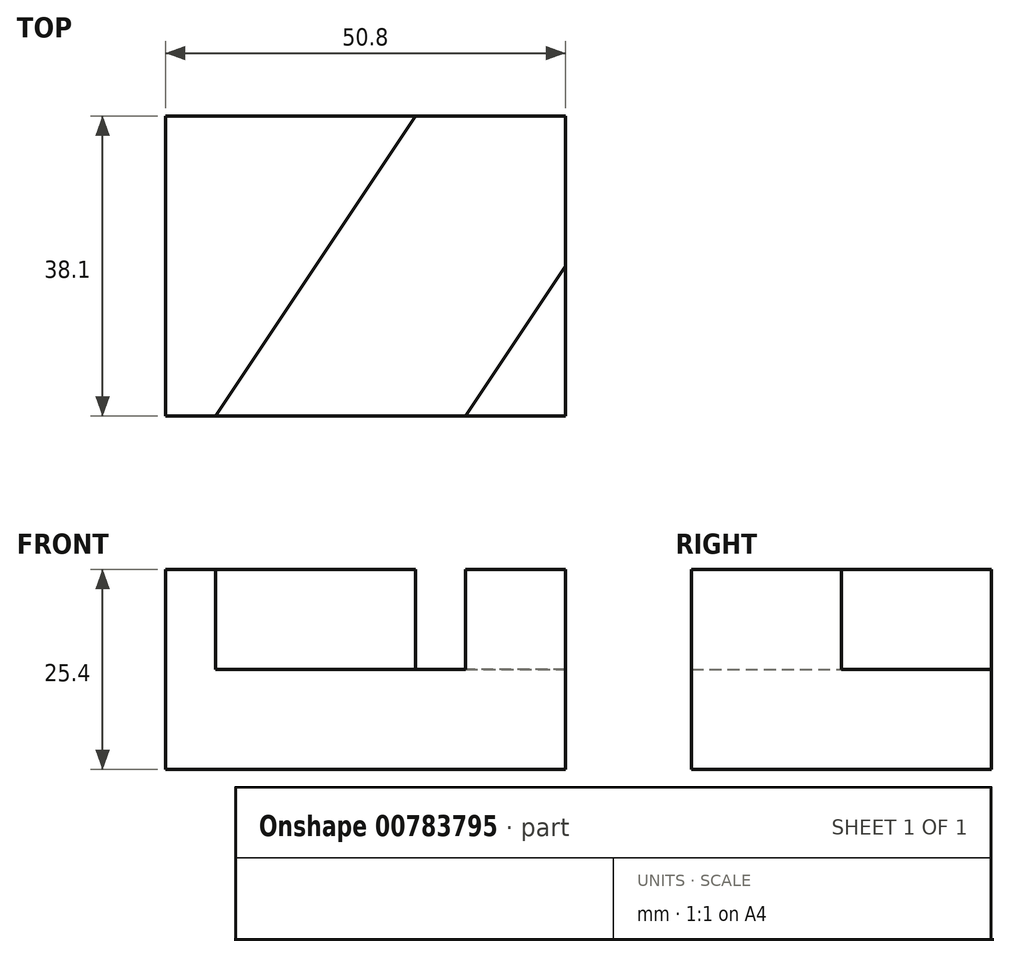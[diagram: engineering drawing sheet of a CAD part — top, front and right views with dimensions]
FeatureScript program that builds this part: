
annotation { "Feature Type Name" : "Feature", "Feature Type Description" : "" }
export const myFeature = defineFeature(function(context is Context, id is Id, definition is map)
    precondition{}
    {
        {
            var Q0;
            Q0=qCreatedBy(makeId("Top.planeOp"),FACE);
            var sketch = newSketch(context, id + "F0", { "sketchPlane" : qUnion([Q0])});
            skLineSegment(sketch, "E0", {"start": v(0, 0) * mm, "end": v(50.8, 0) * mm});
            skLineSegment(sketch, "E1", {"start": v(50.8, 0) * mm, "end": v(50.8, 38.1) * mm});
            skLineSegment(sketch, "E2", {"start": v(50.8, 38.1) * mm, "end": v(0, 38.1) * mm});
            skLineSegment(sketch, "E3", {"start": v(0, 38.1) * mm, "end": v(0, 0) * mm});
            skSolve(sketch);
        }
        {
            var Q0;
            Q0 = qSketchRegion(id + "F0", true);
            extrude(context, id + "F1", {"entities" : qUnion([Q0]), "depth" : 12.7 * mm, "offsetDistance" : 25.4 * mm});
        }
        {
            var Q0;
            Q0=makeQuery(id+"F1.opExtrude","CAP_FACE",FACE,{"disambiguationData":[OSD([sQuery(id+"F0.wireOp",EDGE,"E0"),sQuery(id+"F0.wireOp",EDGE,"E1"),sQuery(id+"F0.wireOp",EDGE,"E2"),sQuery(id+"F0.wireOp",EDGE,"E3")])],"isStart":false});
            var sketch = newSketch(context, id + "F2", { "sketchPlane" : qUnion([Q0])});
            skLineSegment(sketch, "E4", {"start": v(0, 0) * mm, "end": v(6.35, 0) * mm});
            skLineSegment(sketch, "E5", {"start": v(0, 38.1) * mm, "end": v(31.75, 38.1) * mm});
            skLineSegment(sketch, "E6", {"start": v(6.35, 0) * mm, "end": v(31.75, 38.1) * mm});
            skSolve(sketch);
        }
        {
            var Q0;
            Q0=makeQuery(id+"F2.imprint","IMPRINT",FACE,{"disambiguationData":[TD([[makeQuery(id+"F2.imprint","IMPRINT",EDGE,{"derivedFrom":sQuery(id+"F2.wireOp",EDGE,"E4")}),1.0]])]});
            extrude(context, id + "F3", {"entities" : qUnion([Q0]), "operationType" : NewBodyOperationType.ADD, "depth" : 12.7 * mm, "offsetDistance" : 25.4 * mm});
        }
        {
            var Q0;
            Q0=makeQuery(id+"F1.opExtrude","CAP_FACE",FACE,{"disambiguationData":[OSD([sQuery(id+"F0.wireOp",EDGE,"E0"),sQuery(id+"F0.wireOp",EDGE,"E1"),sQuery(id+"F0.wireOp",EDGE,"E2"),sQuery(id+"F0.wireOp",EDGE,"E3")])],"isStart":false});
            var sketch = newSketch(context, id + "F4", { "sketchPlane" : qUnion([Q0])});
            skLineSegment(sketch, "E7", {"start": v(50.8, 0) * mm, "end": v(38.1, 0) * mm});
            skLineSegment(sketch, "E8", {"start": v(50.8, 0) * mm, "end": v(50.8, 19.05) * mm});
            skLineSegment(sketch, "E9", {"start": v(38.1, 0) * mm, "end": v(50.8, 19.05) * mm});
            skSolve(sketch);
        }
        {
            var Q0;
            Q0=makeQuery(id+"F4.imprint","IMPRINT",FACE,{"disambiguationData":[TD([[makeQuery(id+"F4.imprint","IMPRINT",EDGE,{"derivedFrom":sQuery(id+"F4.wireOp",EDGE,"E7")}),1.0]])]});
            extrude(context, id + "F5", {"entities" : qUnion([Q0]), "operationType" : NewBodyOperationType.ADD, "depth" : 12.7 * mm, "offsetDistance" : 25.4 * mm});
        }
    });
